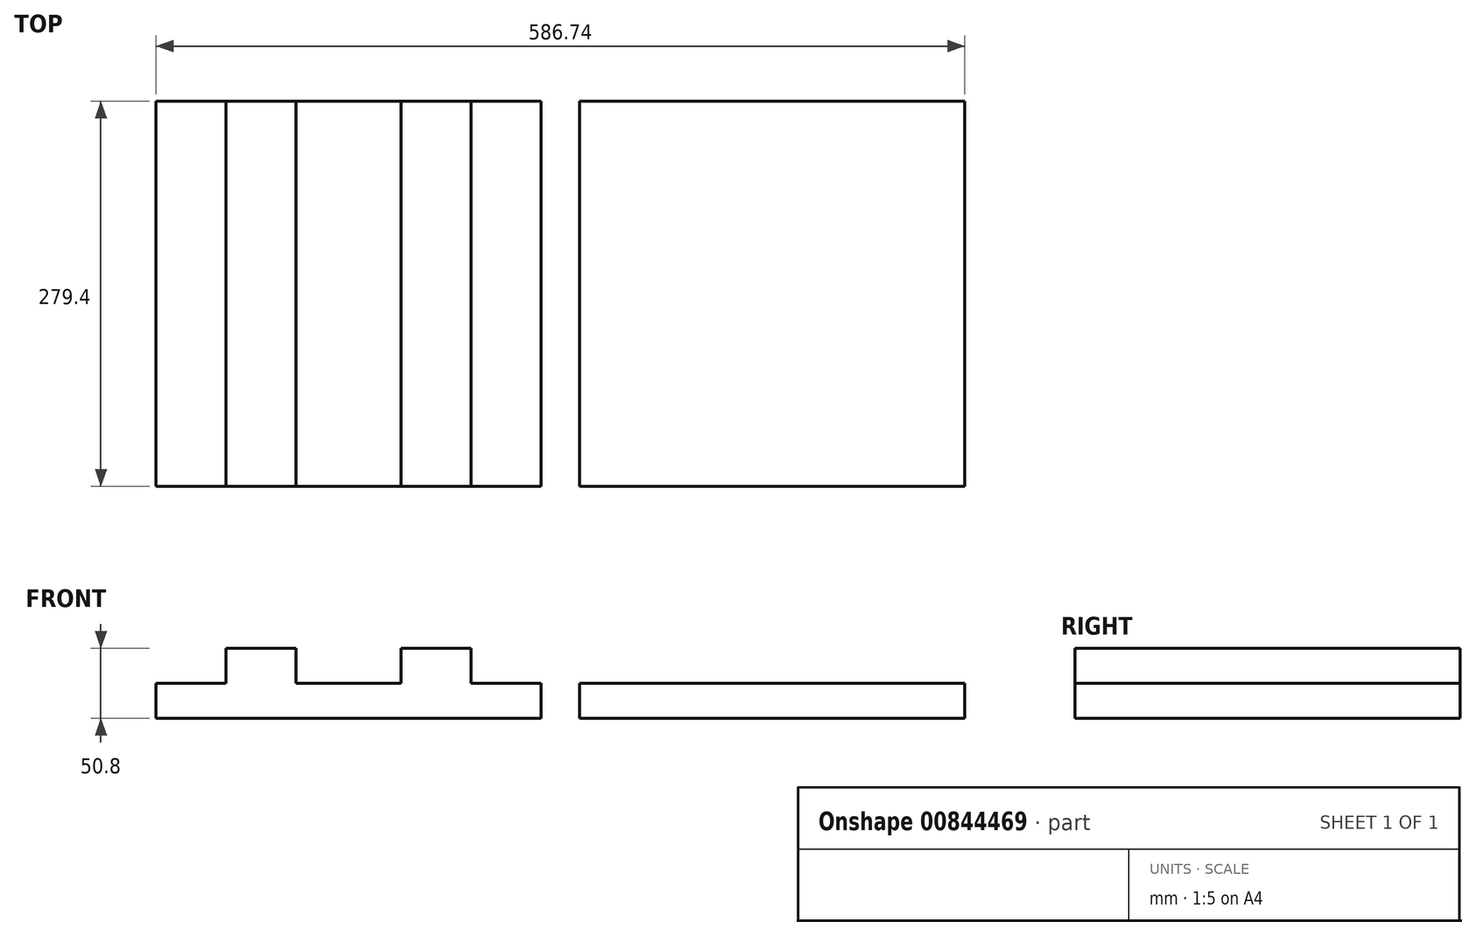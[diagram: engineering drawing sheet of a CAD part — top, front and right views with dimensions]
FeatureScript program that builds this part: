
annotation { "Feature Type Name" : "Feature", "Feature Type Description" : "" }
export const myFeature = defineFeature(function(context is Context, id is Id, definition is map)
    precondition{}
    {
        {
            var Q0;
            Q0=qCreatedBy(makeId("Top.planeOp"),FACE);
            var sketch = newSketch(context, id + "F0", { "sketchPlane" : qUnion([Q0])});
            skLineSegment(sketch, "E0.bottom", {"start": v(-104.13, 167.45) * mm, "end": v(175.27, 167.45) * mm});
            skLineSegment(sketch, "E0.top", {"start": v(-104.13, -111.95) * mm, "end": v(175.27, -111.95) * mm});
            skLineSegment(sketch, "E0.left", {"start": v(-104.13, 167.45) * mm, "end": v(-104.13, -111.95) * mm});
            skLineSegment(sketch, "E0.right", {"start": v(175.27, 167.45) * mm, "end": v(175.27, -111.95) * mm});
            skSolve(sketch);
        }
        {
            var Q0;
            Q0=makeQuery(id+"F0.imprint","IMPRINT",FACE,{"disambiguationData":[TD([[makeQuery(id+"F0.imprint","IMPRINT",EDGE,{"derivedFrom":sQuery(id+"F0.wireOp",EDGE,"E0.bottom")}),-1.0]])]});
            extrude(context, id + "F1", {"entities" : qUnion([Q0]), "depth" : 25.4 * mm, "offsetDistance" : 25.4 * mm});
        }
        {
            var Q0;
            Q0=makeQuery(id+"F1.opExtrude","CAP_FACE",FACE,{"disambiguationData":[OSD([sQuery(id+"F0.wireOp",EDGE,"E0.bottom"),sQuery(id+"F0.wireOp",EDGE,"E0.top"),sQuery(id+"F0.wireOp",EDGE,"E0.left"),sQuery(id+"F0.wireOp",EDGE,"E0.right")])],"isStart":true});
            var sketch = newSketch(context, id + "F2", { "sketchPlane" : qUnion([Q0])});
            skLineSegment(sketch, "E1.bottom", {"start": v(-411.47, 111.95) * mm, "end": v(-132.07, 111.95) * mm});
            skLineSegment(sketch, "E1.top", {"start": v(-411.47, -167.45) * mm, "end": v(-132.07, -167.45) * mm});
            skLineSegment(sketch, "E1.left", {"start": v(-411.47, 111.95) * mm, "end": v(-411.47, -167.45) * mm});
            skLineSegment(sketch, "E1.right", {"start": v(-132.07, 111.95) * mm, "end": v(-132.07, -167.45) * mm});
            skSolve(sketch);
        }
        {
            var Q0;
            Q0=makeQuery(id+"F2.imprint","IMPRINT",FACE,{"disambiguationData":[TD([[makeQuery(id+"F2.imprint","IMPRINT",EDGE,{"derivedFrom":sQuery(id+"F2.wireOp",EDGE,"E1.bottom")}),-1.0]])]});
            extrude(context, id + "F3", {"entities" : qUnion([Q0]), "oppositeDirection" : true, "depth" : 25.4 * mm, "offsetDistance" : 25.4 * mm});
        }
        {
            var Q0;
            Q0=makeQuery(id+"F3.opExtrude","CAP_FACE",FACE,{"disambiguationData":[OSD([sQuery(id+"F2.wireOp",EDGE,"E1.bottom"),sQuery(id+"F2.wireOp",EDGE,"E1.top"),sQuery(id+"F2.wireOp",EDGE,"E1.left"),sQuery(id+"F2.wireOp",EDGE,"E1.right")])],"isStart":false});
            var sketch = newSketch(context, id + "F4", { "sketchPlane" : qUnion([Q0])});
            skLineSegment(sketch, "E2.bottom", {"start": v(-360.67, 167.45) * mm, "end": v(-309.87, 167.45) * mm});
            skLineSegment(sketch, "E2.top", {"start": v(-360.67, -111.95) * mm, "end": v(-309.87, -111.95) * mm});
            skLineSegment(sketch, "E2.left", {"start": v(-360.67, 167.45) * mm, "end": v(-360.67, -111.95) * mm});
            skLineSegment(sketch, "E2.right", {"start": v(-309.87, 167.45) * mm, "end": v(-309.87, -111.95) * mm});
            skLineSegment(sketch, "E3.bottom", {"start": v(-233.67, 167.45) * mm, "end": v(-182.87, 167.45) * mm});
            skLineSegment(sketch, "E3.top", {"start": v(-233.67, -111.95) * mm, "end": v(-182.87, -111.95) * mm});
            skLineSegment(sketch, "E3.left", {"start": v(-233.67, 167.45) * mm, "end": v(-233.67, -111.95) * mm});
            skLineSegment(sketch, "E3.right", {"start": v(-182.87, 167.45) * mm, "end": v(-182.87, -111.95) * mm});
            skSolve(sketch);
        }
        {
            var Q0;
            Q0=makeQuery(id+"F4.imprint","IMPRINT",FACE,{"disambiguationData":[TD([[makeQuery(id+"F4.imprint","IMPRINT",EDGE,{"derivedFrom":sQuery(id+"F4.wireOp",EDGE,"E2.bottom")}),-1.0]])]});
            var Q1;
            Q1=makeQuery(id+"F4.imprint","IMPRINT",FACE,{"disambiguationData":[TD([[makeQuery(id+"F4.imprint","IMPRINT",EDGE,{"derivedFrom":sQuery(id+"F4.wireOp",EDGE,"E3.bottom")}),-1.0]])]});
            extrude(context, id + "F5", {"entities" : qUnion([Q0, Q1]), "operationType" : NewBodyOperationType.ADD, "depth" : 25.4 * mm, "offsetDistance" : 25.4 * mm});
        }
    });
